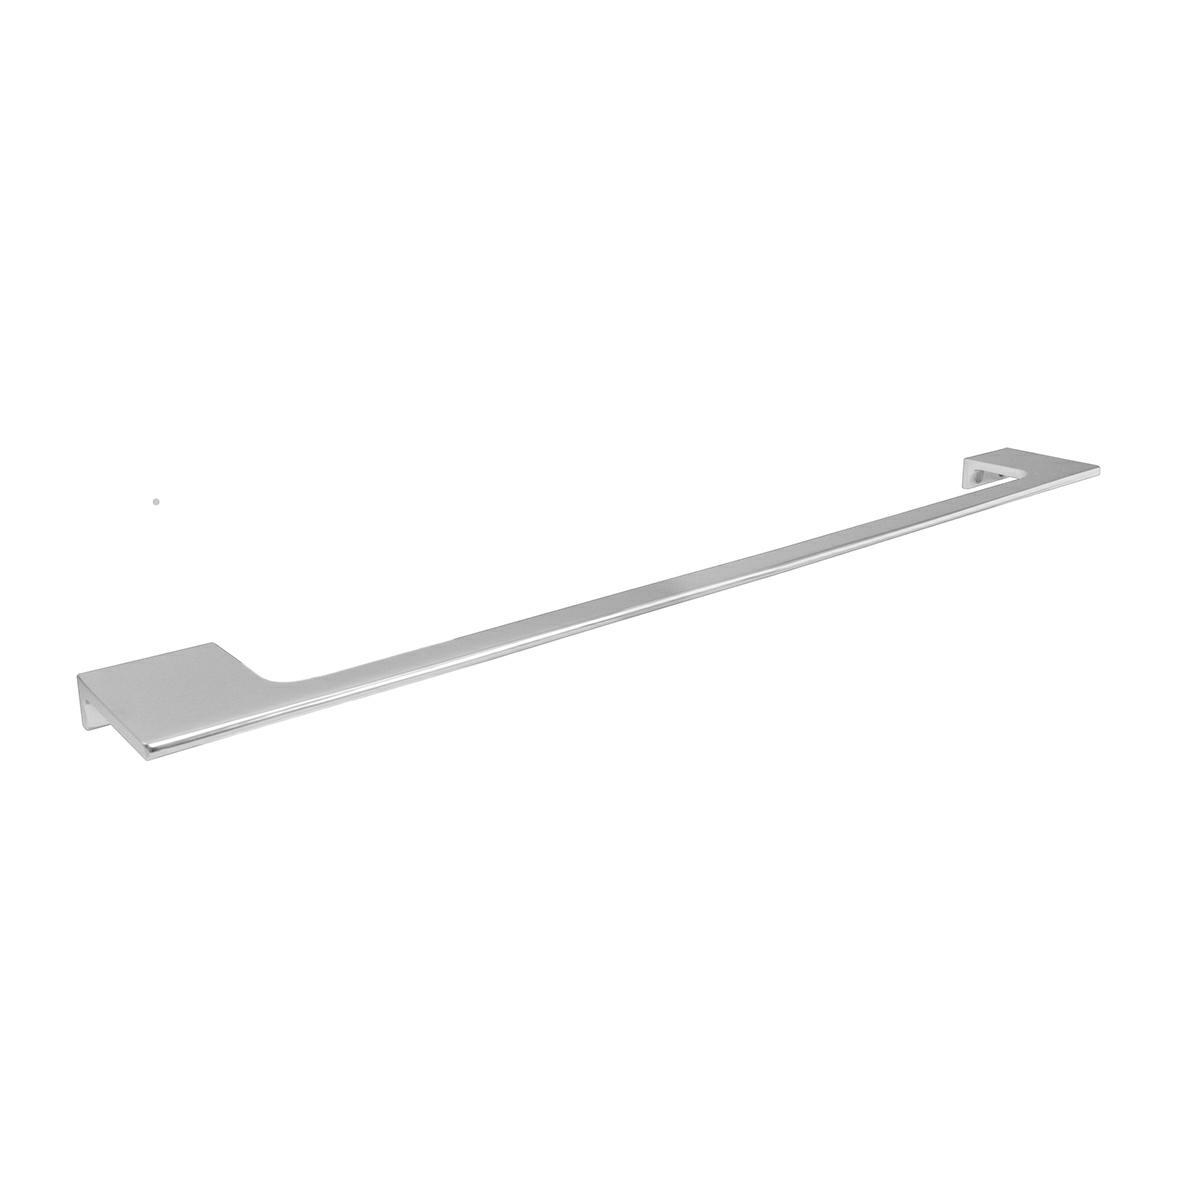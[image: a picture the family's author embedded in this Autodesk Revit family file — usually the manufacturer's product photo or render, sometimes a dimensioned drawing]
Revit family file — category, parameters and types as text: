
# Revit family: ACC-105
name_source: partatom
category: Aparatos sanitarios
units: mm (PartAtom-declared; Revit-internal decimal feet)

## family parameters
Compartido = No
Corte con vacíos al cargar = No
Cota de conector redondo = Diámetro de uso
Número OmniClass = 23.45.00.00
Punto de cálculo de habitación = No
Se basa en plano de trabajo = No
Siempre vertical = Sí
Tipo de pieza = Normal
Título OmniClass = Sanitary, Laundry, and Cleaning Equipment

## types (2) — shared parameters
Brass Chromed = Brass
Comentarios de tipo = Accesories
Elevación por defecto = 0"
Fabricante = HELVEX
Total Depth = 3"

## per-type parameters (varying)
| type | Data Sheet | Descripción | Features | Imagen de tipo | Instructive | Total Length | Total Support Diameter | URL | Ébano |
| 14104 | http://helvex.com | Kúbica Paper Holder | Wall Mounted Accessory; Setting Kit Included; Includes Fastening Tool | <Ninguno> | http://helvex.com | 8" | 2" | http://helvex.com | <Por categoría> |
| ACC-105 | https://www.helvex.com.mx | Toallero de barra Access | Bar towel rack Accessed. | ACC-105.jpg | https://www.helvex.com.mx | 24" | 1" | https://www.helvex.com.mx | Ébano |

note: column(s) folded — value = type name in every type: Modelo

## geometry (parser evidence)
native form markers: Sweep x3
no freeform markers — native parametric forms only
